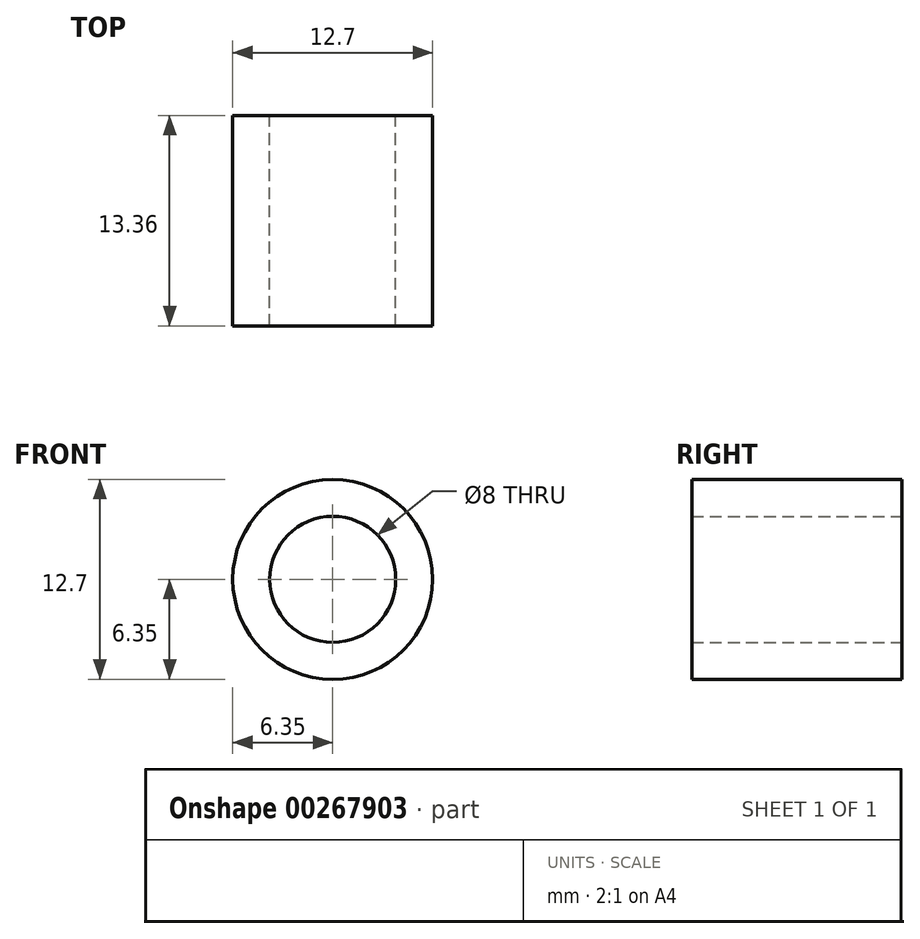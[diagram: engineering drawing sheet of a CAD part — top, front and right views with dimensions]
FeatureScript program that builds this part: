
annotation { "Feature Type Name" : "Feature", "Feature Type Description" : "" }
export const myFeature = defineFeature(function(context is Context, id is Id, definition is map)
    precondition{}
    {
        {
            var Q0;
            Q0=qCreatedBy(makeId("Front.planeOp"),FACE);
            var sketch = newSketch(context, id + "F0", { "sketchPlane" : qUnion([Q0])});
            skCircle(sketch, "E0", {"center": v(0, 0) * mm, "radius": 6.35 * mm});
            skCircle(sketch, "E1", {"center": v(0, 0) * mm, "radius": 4 * mm});
            skSolve(sketch);
        }
        {
            var Q0;
            Q0=makeQuery(id+"F0.imprint","IMPRINT",FACE,{"disambiguationData":[TD([[makeQuery(id+"F0.imprint","IMPRINT",EDGE,{"derivedFrom":sQuery(id+"F0.wireOp",EDGE,"E0")}),1.0]])]});
            extrude(context, id + "F1", {"entities" : qUnion([Q0]), "depth" : 13.36 * mm});
        }
    });
